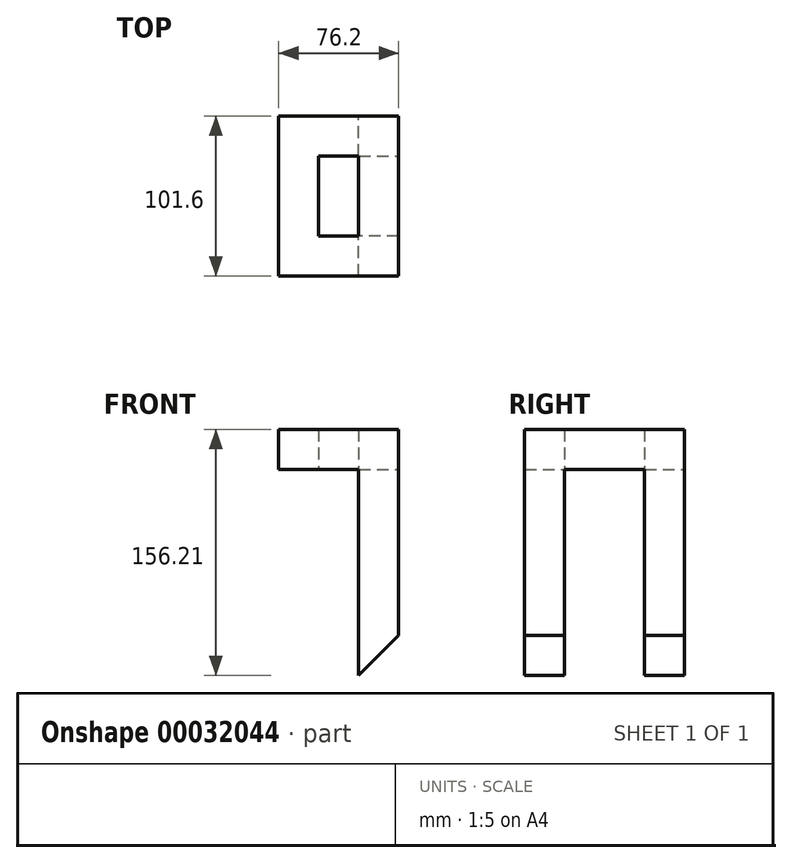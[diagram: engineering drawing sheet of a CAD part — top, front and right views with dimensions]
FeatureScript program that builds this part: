
annotation { "Feature Type Name" : "Feature", "Feature Type Description" : "" }
export const myFeature = defineFeature(function(context is Context, id is Id, definition is map)
    precondition{}
    {
        {
            var Q0;
            Q0=qCreatedBy(makeId("Right.planeOp"),FACE);
            var sketch = newSketch(context, id + "F0", { "sketchPlane" : qUnion([Q0])});
            skLineSegment(sketch, "E0.bottom", {"start": v(50.8, 12.7) * mm, "end": v(-50.8, 12.7) * mm});
            skLineSegment(sketch, "E0.top", {"start": v(50.8, -12.7) * mm, "end": v(-50.8, -12.7) * mm});
            skLineSegment(sketch, "E0.left", {"start": v(50.8, 12.7) * mm, "end": v(50.8, -12.7) * mm});
            skLineSegment(sketch, "E0.right", {"start": v(-50.8, 12.7) * mm, "end": v(-50.8, -12.7) * mm});
            skPoint(sketch, "E0.middle", {"position": v(0, 0) * mm});
            skSolve(sketch);
        }
        {
            var Q0;
            Q0=makeQuery(id+"F0.imprint","IMPRINT",FACE,{"disambiguationData":[TD([[makeQuery(id+"F0.imprint","IMPRINT",EDGE,{"derivedFrom":sQuery(id+"F0.wireOp",EDGE,"E0.bottom")}),1.0]])]});
            extrude(context, id + "F1", {"entities" : qUnion([Q0]), "depth" : 25.4 * mm});
        }
        {
            var Q0;
            Q0=makeQuery(id+"F1.opExtrude","CAP_FACE",FACE,{"disambiguationData":[OSD([sQuery(id+"F0.wireOp",EDGE,"E0.bottom"),sQuery(id+"F0.wireOp",EDGE,"E0.top"),sQuery(id+"F0.wireOp",EDGE,"E0.left"),sQuery(id+"F0.wireOp",EDGE,"E0.right")])],"isStart":false});
            var sketch = newSketch(context, id + "F2", { "sketchPlane" : qUnion([Q0])});
            skLineSegment(sketch, "E1.bottom", {"start": v(-50.8, 12.7) * mm, "end": v(-25.4, 12.7) * mm});
            skLineSegment(sketch, "E1.top", {"start": v(-50.8, -12.7) * mm, "end": v(-25.4, -12.7) * mm});
            skLineSegment(sketch, "E1.left", {"start": v(-50.8, 12.7) * mm, "end": v(-50.8, -12.7) * mm});
            skLineSegment(sketch, "E1.right", {"start": v(-25.4, 12.7) * mm, "end": v(-25.4, -12.7) * mm});
            skLineSegment(sketch, "E2.bottom", {"start": v(50.8, 12.7) * mm, "end": v(25.4, 12.7) * mm});
            skLineSegment(sketch, "E2.top", {"start": v(50.8, -12.7) * mm, "end": v(25.4, -12.7) * mm});
            skLineSegment(sketch, "E2.left", {"start": v(50.8, 12.7) * mm, "end": v(50.8, -12.7) * mm});
            skLineSegment(sketch, "E2.right", {"start": v(25.4, 12.7) * mm, "end": v(25.4, -12.7) * mm});
            skSolve(sketch);
        }
        {
            var Q0;
            Q0=makeQuery(id+"F2.imprint","IMPRINT",FACE,{"disambiguationData":[TD([[makeQuery(id+"F2.imprint","IMPRINT",EDGE,{"derivedFrom":sQuery(id+"F2.wireOp",EDGE,"E2.bottom")}),1.0]])]});
            var Q1;
            Q1=makeQuery(id+"F2.imprint","IMPRINT",FACE,{"disambiguationData":[TD([[makeQuery(id+"F2.imprint","IMPRINT",EDGE,{"derivedFrom":sQuery(id+"F2.wireOp",EDGE,"E1.bottom")}),1.0]])]});
            extrude(context, id + "F3", {"entities" : qUnion([Q0, Q1]), "operationType" : NewBodyOperationType.ADD, "depth" : 25.4 * mm});
        }
        {
            var Q0;
            Q0=makeQuery(id+"F3.opExtrude","CAP_FACE",FACE,{"disambiguationData":[OSD([sQuery(id+"F2.wireOp",EDGE,"E1.bottom"),sQuery(id+"F2.wireOp",EDGE,"E1.top"),sQuery(id+"F2.wireOp",EDGE,"E1.left"),sQuery(id+"F2.wireOp",EDGE,"E1.right")])],"isStart":false});
            var sketch = newSketch(context, id + "F4", { "sketchPlane" : qUnion([Q0])});
            skLineSegment(sketch, "E3.bottom", {"start": v(-50.8, 12.7) * mm, "end": v(50.8, 12.7) * mm});
            skLineSegment(sketch, "E3.top", {"start": v(-50.8, -12.7) * mm, "end": v(50.8, -12.7) * mm});
            skLineSegment(sketch, "E3.left", {"start": v(-50.8, 12.7) * mm, "end": v(-50.8, -12.7) * mm});
            skLineSegment(sketch, "E3.right", {"start": v(50.8, 12.7) * mm, "end": v(50.8, -12.7) * mm});
            skSolve(sketch);
        }
        {
            var Q0;
            {var subQ2=sQuery(id+"F4.wireOp",EDGE,"E3.right");Q0=makeQuery(id+"F4.imprint","IMPRINT",FACE,{"disambiguationData":[TD([[makeQuery(id+"F4.imprint","IMPRINT",EDGE,{"derivedFrom":subQ2}),-1.0]])]});}
            var Q1;
            {var subQ0=sQuery(id+"F4.wireOp",EDGE,"E3.left");Q1=makeQuery(id+"F4.imprint","IMPRINT",FACE,{"disambiguationData":[TD([[makeQuery(id+"F4.imprint","IMPRINT",EDGE,{"derivedFrom":subQ0}),1.0]])]});}
            extrude(context, id + "F5", {"entities" : qUnion([Q0, Q1]), "operationType" : NewBodyOperationType.ADD, "depth" : 25.4 * mm});
        }
        {
            var Q0;
            Q0=makeQuery(id+"F5.boolean.opBoolean","MERGE",FACE,{"derivedFrom":[makeQuery(id+"F3.boolean.opBoolean","MERGE",FACE,{"derivedFrom":[makeQuery(id+"F1.opExtrude","SWEPT_FACE",FACE,{"disambiguationData":[OSD([sQuery(id+"F0.wireOp",EDGE,"E0.top")])]}),makeQuery(id+"F3.opExtrude","SWEPT_FACE",FACE,{"disambiguationData":[OSD([sQuery(id+"F2.wireOp",EDGE,"E1.top")])]}),makeQuery(id+"F3.opExtrude","SWEPT_FACE",FACE,{"disambiguationData":[OSD([sQuery(id+"F2.wireOp",EDGE,"E2.top")])]})]}),makeQuery(id+"F5.opExtrude","SWEPT_FACE",FACE,{"disambiguationData":[OSD([sQuery(id+"F4.wireOp",EDGE,"E3.top")])]})]});
            var sketch = newSketch(context, id + "F6", { "sketchPlane" : qUnion([Q0])});
            skLineSegment(sketch, "E4.bottom", {"start": v(76.2, 50.8) * mm, "end": v(50.8, 50.8) * mm});
            skLineSegment(sketch, "E4.top", {"start": v(76.2, 25.4) * mm, "end": v(50.8, 25.4) * mm});
            skLineSegment(sketch, "E4.left", {"start": v(76.2, 50.8) * mm, "end": v(76.2, 25.4) * mm});
            skLineSegment(sketch, "E4.right", {"start": v(50.8, 50.8) * mm, "end": v(50.8, 25.4) * mm});
            skLineSegment(sketch, "E5.bottom", {"start": v(50.8, -25.4) * mm, "end": v(76.2, -25.4) * mm});
            skLineSegment(sketch, "E5.top", {"start": v(50.8, -50.8) * mm, "end": v(76.2, -50.8) * mm});
            skLineSegment(sketch, "E5.left", {"start": v(50.8, -25.4) * mm, "end": v(50.8, -50.8) * mm});
            skLineSegment(sketch, "E5.right", {"start": v(76.2, -25.4) * mm, "end": v(76.2, -50.8) * mm});
            skSolve(sketch);
        }
        {
            var Q0;
            Q0=makeQuery(id+"F6.imprint","IMPRINT",FACE,{"disambiguationData":[TD([[makeQuery(id+"F6.imprint","IMPRINT",EDGE,{"derivedFrom":sQuery(id+"F6.wireOp",EDGE,"E4.bottom")}),1.0]])]});
            var Q1;
            Q1=makeQuery(id+"F6.imprint","IMPRINT",FACE,{"disambiguationData":[TD([[makeQuery(id+"F6.imprint","IMPRINT",EDGE,{"derivedFrom":sQuery(id+"F6.wireOp",EDGE,"E5.bottom")}),-1.0]])]});
            extrude(context, id + "F7", {"entities" : qUnion([Q0, Q1]), "operationType" : NewBodyOperationType.ADD, "depth" : 156.21 * mm});
        }
        {
            var Q0;
            Q0=makeQuery(id+"F7.opExtrude","CAP_EDGE",EDGE,{"disambiguationData":[OSD([sQuery(id+"F6.wireOp",EDGE,"E5.right")])],"isStart":false});
            var Q1;
            Q1=makeQuery(id+"F7.opExtrude","CAP_EDGE",EDGE,{"disambiguationData":[OSD([sQuery(id+"F6.wireOp",EDGE,"E4.left")])],"isStart":false});
            chamfer(context, id + "F8", {"entities" : qUnion([Q0, Q1]), "chamferType" : ChamferType.OFFSET_ANGLE, "width" : 50.8 * mm, "oppositeDirection" : false, "angle" : 45 * degree, "tangentPropagation" : true});
        }
    });
